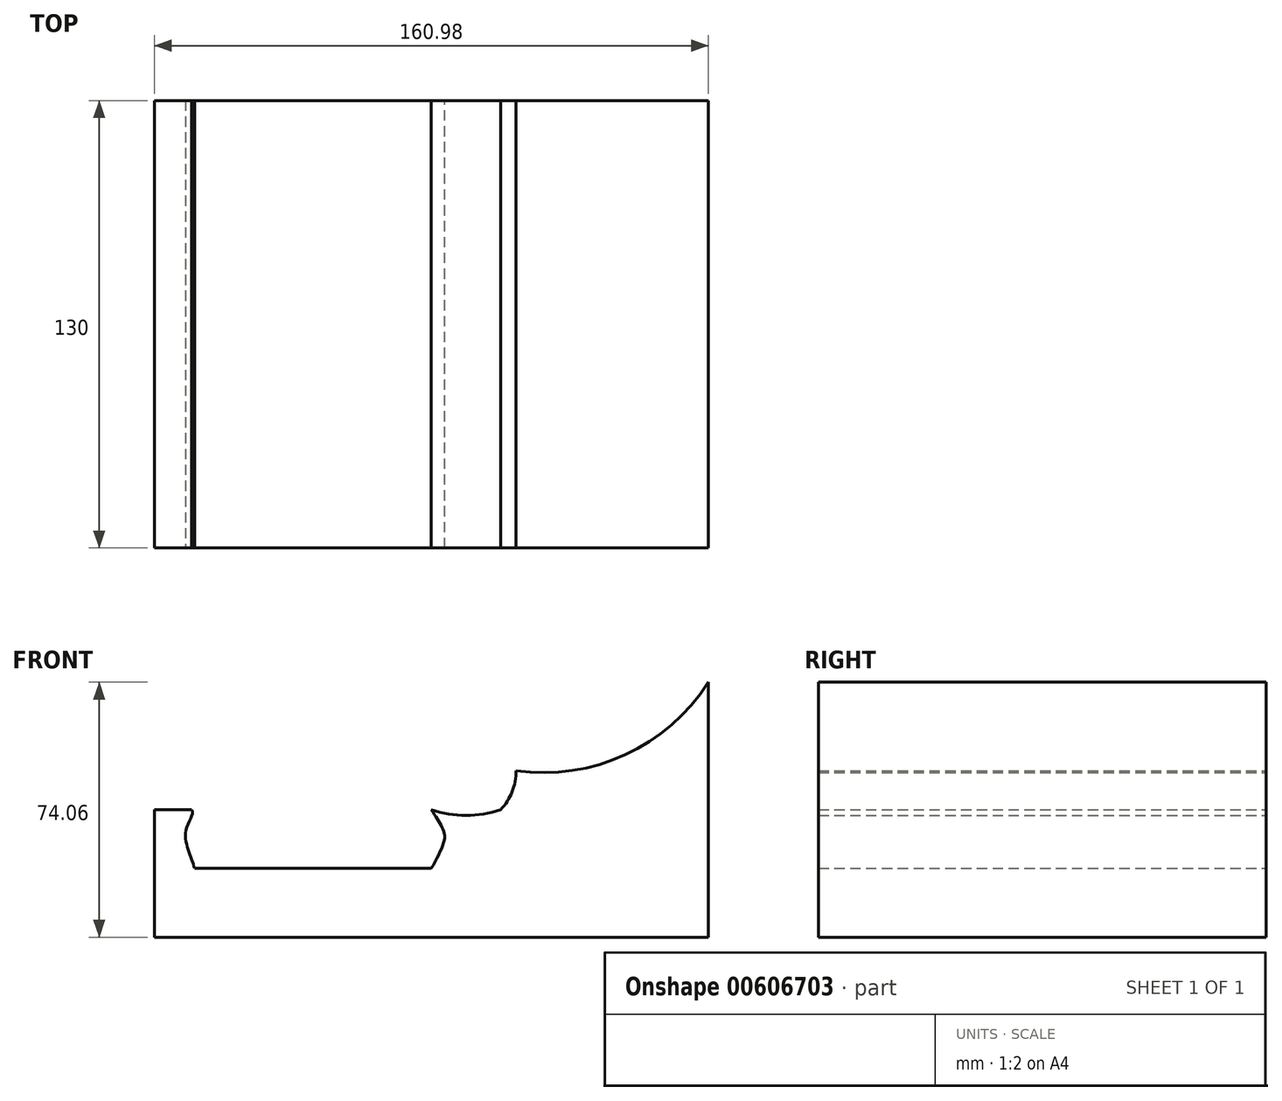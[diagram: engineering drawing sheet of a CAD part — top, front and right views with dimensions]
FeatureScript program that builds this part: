
annotation { "Feature Type Name" : "Feature", "Feature Type Description" : "" }
export const myFeature = defineFeature(function(context is Context, id is Id, definition is map)
    precondition{}
    {
        {
            var Q0;
            Q0=qCreatedBy(makeId("Front.planeOp"),FACE);
            var sketch = newSketch(context, id + "F0", { "sketchPlane" : qUnion([Q0])});
            skLineSegment(sketch, "E0.top", {"start": v(-80.49, -37.03) * mm, "end": v(80.49, -37.03) * mm});
            skLineSegment(sketch, "E0.left", {"start": v(-80.49, 0) * mm, "end": v(-80.49, -37.03) * mm});
            skLineSegment(sketch, "E0.right", {"start": v(80.49, 37.03) * mm, "end": v(80.49, -37.03) * mm});
            skPoint(sketch, "E0.middle", {"position": v(0, 0) * mm});
            skLineSegment(sketch, "E1", {"start": v(-69.6, 0) * mm, "end": v(-80.49, 0) * mm});
            skPoint(sketch, "E2.orphan", {"position": v(-80.49, 37.03) * mm});
            skLineSegment(sketch, "E3", {"start": v(0, -17.06) * mm, "end": v(-68.78, -17.06) * mm});
            skFitSpline(sketch, "E4", {"points": [v(-80.49, 0) * mm, v(-69.6, 0) * mm, v(-71.23, -5.65) * mm, v(-70.41, -12.17) * mm, v(-68.78, -17.06) * mm], "startDerivative": vector(34.36, 6.04) * mm, "endDerivative": vector(6.84, -20.41) * mm});
            skPoint(sketch, "E5.end.orphan", {"position": v(0, 37.03) * mm});
            skArc(sketch, "E6", {"start": v(24.59, 11.31) * mm, "mid": v(56.31, 15.96) * mm, "end": v(80.49, 37.03) * mm});
            skArc(sketch, "E7", {"start": v(20.1, 0) * mm, "mid": v(23.46, 5.21) * mm, "end": v(24.59, 11.31) * mm});
            skArc(sketch, "E8", {"start": v(0, 0) * mm, "mid": v(10.05, -1.63) * mm, "end": v(20.1, 0) * mm});
            skPoint(sketch, "E9.2.internal.snap0", {"position": v(0, -8.53) * mm});
            skFitSpline(sketch, "E9", {"points": [v(0, 0) * mm, v(2.97, -4.83) * mm, v(3.79, -8.53) * mm, v(0, -17.06) * mm], "startDerivative": vector(10.3, -15.62) * mm, "endDerivative": vector(-12.63, -22.8) * mm});
            skSolve(sketch);
        }
        {
            var Q0;
            Q0=makeQuery(id+"F0.imprint","IMPRINT",FACE,{"disambiguationData":[TD([[makeQuery(id+"F0.imprint","IMPRINT",EDGE,{"derivedFrom":sQuery(id+"F0.wireOp",EDGE,"E0.top")}),1.0]])]});
            extrude(context, id + "F1", {"entities" : qUnion([Q0]), "depth" : 130 * mm, "offsetDistance" : 25.4 * mm});
        }
    });
